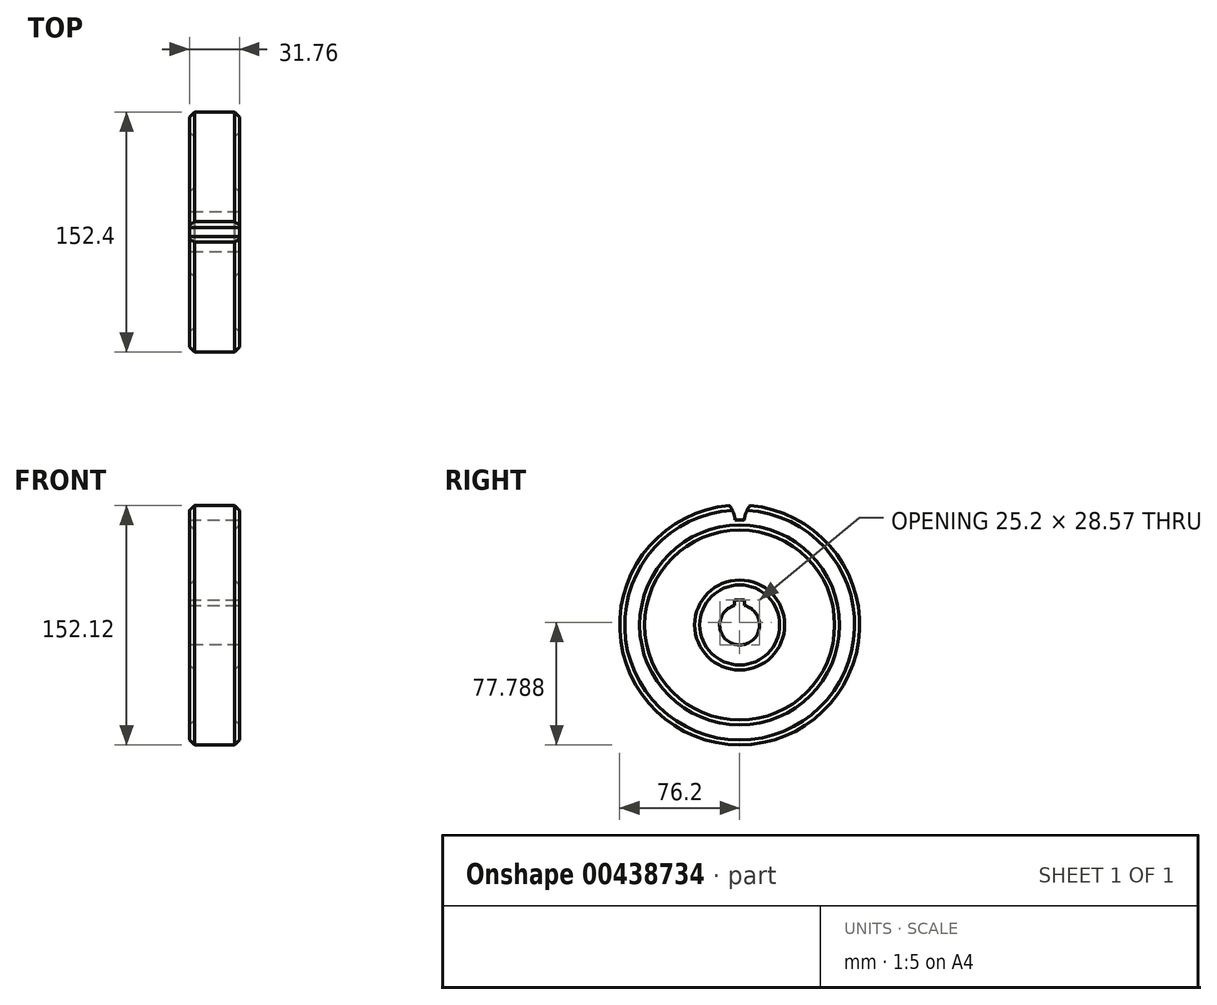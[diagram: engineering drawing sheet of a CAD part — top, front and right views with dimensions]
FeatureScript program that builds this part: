
annotation { "Feature Type Name" : "Feature", "Feature Type Description" : "" }
export const myFeature = defineFeature(function(context is Context, id is Id, definition is map)
    precondition{}
    {
        {
            var Q0;
            Q0=qCreatedBy(makeId("Front.planeOp"),FACE);
            var sketch = newSketch(context, id + "F0", { "sketchPlane" : qUnion([Q0])});
            skLineSegment(sketch, "E0", {"start": v(0, -28.27) * mm, "end": v(0, 35.23) * mm});
            skLineSegment(sketch, "E1", {"start": v(0, 35.23) * mm, "end": v(12.7, 35.23) * mm});
            skLineSegment(sketch, "E2", {"start": v(12.7, 35.23) * mm, "end": v(15.87, 32.06) * mm});
            skLineSegment(sketch, "E3", {"start": v(15.87, 32.06) * mm, "end": v(15.87, 22.53) * mm});
            skLineSegment(sketch, "E4", {"start": v(15.87, 22.53) * mm, "end": v(12.7, 19.36) * mm});
            skLineSegment(sketch, "E5", {"start": v(12.7, 19.36) * mm, "end": v(12.7, -12.4) * mm});
            skLineSegment(sketch, "E6", {"start": v(12.7, -12.4) * mm, "end": v(15.87, -15.57) * mm});
            skLineSegment(sketch, "E7", {"start": v(15.87, -15.57) * mm, "end": v(15.87, -28.27) * mm});
            skLineSegment(sketch, "E8", {"start": v(15.87, -28.27) * mm, "end": v(0, -28.27) * mm});
            skLineSegment(sketch, "E9", {"start": v(0, -28.27) * mm, "end": v(0, -40.97) * mm});
            skLineSegment(sketch, "E10", {"start": v(0, -40.97) * mm, "end": v(17.78, -40.97) * mm});
            skLineSegment(sketch, "E11.MirrorCS", {"start": v(0, 35.23) * mm, "end": v(-12.7, 35.23) * mm});
            skLineSegment(sketch, "E12.MirrorCS", {"start": v(-12.7, 35.23) * mm, "end": v(-15.88, 32.06) * mm});
            skLineSegment(sketch, "E13.MirrorCS", {"start": v(-15.88, 32.06) * mm, "end": v(-15.87, 22.53) * mm});
            skLineSegment(sketch, "E14.MirrorCS", {"start": v(-15.87, 22.53) * mm, "end": v(-12.7, 19.36) * mm});
            skLineSegment(sketch, "E15.MirrorCS", {"start": v(-12.7, 19.36) * mm, "end": v(-12.7, -12.4) * mm});
            skLineSegment(sketch, "E16.MirrorCS", {"start": v(-15.87, -15.57) * mm, "end": v(-15.87, -28.27) * mm});
            skLineSegment(sketch, "E17.MirrorCS", {"start": v(-12.7, -12.4) * mm, "end": v(-15.88, -15.57) * mm});
            skLineSegment(sketch, "E18.MirrorCS", {"start": v(-15.88, -28.27) * mm, "end": v(0, -28.27) * mm});
            skSolve(sketch);
        }
        {
            var Q0;
            Q0=makeQuery(id+"F0.imprint","IMPRINT",FACE,{"disambiguationData":[TD([[makeQuery(id+"F0.imprint","IMPRINT",EDGE,{"derivedFrom":sQuery(id+"F0.wireOp",EDGE,"E0")}),-1.0]])]});
            var Q1;
            Q1=makeQuery(id+"F0.imprint","IMPRINT",FACE,{"disambiguationData":[TD([[makeQuery(id+"F0.imprint","IMPRINT",EDGE,{"derivedFrom":sQuery(id+"F0.wireOp",EDGE,"E0")}),1.0]])]});
            var Q2;
            Q2=sQuery(id+"F0.wireOp",EDGE,"E10");
            revolve(context, id + "F1", {"entities" : qUnion([Q0, Q1]), "axis" : qUnion([Q2]), "revolveType" : RevolveType.FULL});
        }
        {
            var Q0;
            Q0=makeQuery(id+"F1.opRevolve","SWEPT_FACE",FACE,{"disambiguationData":[OSD([sQuery(id+"F0.wireOp",EDGE,"E3")])]});
            var sketch = newSketch(context, id + "F2", { "sketchPlane" : qUnion([Q0])});
            skLineSegment(sketch, "E19", {"start": v(0, -40.97) * mm, "end": v(0, 69.87) * mm});
            skArc(sketch, "E20.0", {"start": v(6.54, 34.95) * mm, "mid": v(0, 35.23) * mm, "end": v(-6.54, 34.95) * mm});
            skArc(sketch, "E21", {"start": v(6.54, 34.95) * mm, "mid": v(4.08, 30.57) * mm, "end": v(2.86, 25.7) * mm});
            skLineSegment(sketch, "E22", {"start": v(2.86, 25.7) * mm, "end": v(0, 25.7) * mm});
            skLineSegment(sketch, "E23.MirrorCS", {"start": v(-2.86, 25.7) * mm, "end": v(0, 25.7) * mm});
            skArc(sketch, "E24.MirrorCS", {"start": v(-6.54, 34.95) * mm, "mid": v(-4.08, 30.57) * mm, "end": v(-2.86, 25.7) * mm});
            skSolve(sketch);
        }
        {
            var Q0;
            {var subQ0=sQuery(id+"F2.wireOp",EDGE,"E20.0");var subQ5=sQuery(id+"F2.wireOp",EDGE,"E24.MirrorCS");var subQ6=makeQuery(id+"F2.imprint","INTERSECT",VERTEX,{"derivedFrom":[subQ0,subQ5]});Q0=makeQuery(id+"F2.imprint","IMPRINT",FACE,{"disambiguationData":[TD([[makeQuery(id+"F2.imprint","IMPRINT",EDGE,{"disambiguationData":[TD([[subQ6,1.0]])],"derivedFrom":subQ0}),1.0]])]});}
            var Q1;
            {var subQ0=sQuery(id+"F2.wireOp",EDGE,"E20.0");var subQ5=sQuery(id+"F2.wireOp",EDGE,"E21");var subQ6=makeQuery(id+"F2.imprint","INTERSECT",VERTEX,{"derivedFrom":[subQ0,subQ5]});Q1=makeQuery(id+"F2.imprint","IMPRINT",FACE,{"disambiguationData":[TD([[makeQuery(id+"F2.imprint","IMPRINT",EDGE,{"disambiguationData":[TD([[subQ6,-1.0]])],"derivedFrom":subQ0}),1.0]])]});}
            var Q2;
            {var subQ0=sQuery(id+"F2.wireOp",EDGE,"E22");Q2=makeQuery(id+"F2.imprint","IMPRINT",FACE,{"disambiguationData":[TD([[makeQuery(id+"F2.imprint","IMPRINT",EDGE,{"derivedFrom":subQ0}),-1.0]])]});}
            var Q3;
            {var subQ0=sQuery(id+"F2.wireOp",EDGE,"E23.MirrorCS");Q3=makeQuery(id+"F2.imprint","IMPRINT",FACE,{"disambiguationData":[TD([[makeQuery(id+"F2.imprint","IMPRINT",EDGE,{"derivedFrom":subQ0}),1.0]])]});}
            extrude(context, id + "F3", {"entities" : qUnion([Q0, Q1, Q2, Q3]), "operationType" : NewBodyOperationType.REMOVE, "endBound" : BoundingType.THROUGH_ALL, "oppositeDirection" : true, "depth" : 25.4 * mm});
        }
        {
            var Q0;
            Q0=makeQuery(id+"F1.opRevolve","SWEPT_FACE",FACE,{"disambiguationData":[OSD([sQuery(id+"F0.wireOp",EDGE,"E7")])]});
            var sketch = newSketch(context, id + "F4", { "sketchPlane" : qUnion([Q0])});
            skLineSegment(sketch, "E25", {"start": v(0, -40.97) * mm, "end": v(0, 78.83) * mm});
            skLineSegment(sketch, "E26", {"start": v(0, -25.1) * mm, "end": v(3.18, -25.1) * mm});
            skLineSegment(sketch, "E27", {"start": v(3.17, -25.1) * mm, "end": v(3.18, -28.67) * mm});
            skArc(sketch, "E28.0", {"start": v(3.17, -28.67) * mm, "mid": v(0, -28.27) * mm, "end": v(-3.17, -28.67) * mm});
            skLineSegment(sketch, "E29.MirrorCS", {"start": v(0, -25.1) * mm, "end": v(-3.18, -25.1) * mm});
            skLineSegment(sketch, "E30.MirrorCS", {"start": v(-3.18, -25.1) * mm, "end": v(-3.17, -28.67) * mm});
            skSolve(sketch);
        }
        {
            var Q0;
            {var subQ0=sQuery(id+"F4.wireOp",EDGE,"E26");Q0=makeQuery(id+"F4.imprint","IMPRINT",FACE,{"disambiguationData":[TD([[makeQuery(id+"F4.imprint","IMPRINT",EDGE,{"derivedFrom":subQ0}),-1.0]])]});}
            var Q1;
            {var subQ0=sQuery(id+"F4.wireOp",EDGE,"E29.MirrorCS");Q1=makeQuery(id+"F4.imprint","IMPRINT",FACE,{"disambiguationData":[TD([[makeQuery(id+"F4.imprint","IMPRINT",EDGE,{"derivedFrom":subQ0}),1.0]])]});}
            extrude(context, id + "F5", {"entities" : qUnion([Q0, Q1]), "operationType" : NewBodyOperationType.REMOVE, "endBound" : BoundingType.THROUGH_ALL, "oppositeDirection" : true, "depth" : 25.4 * mm});
        }
    });
